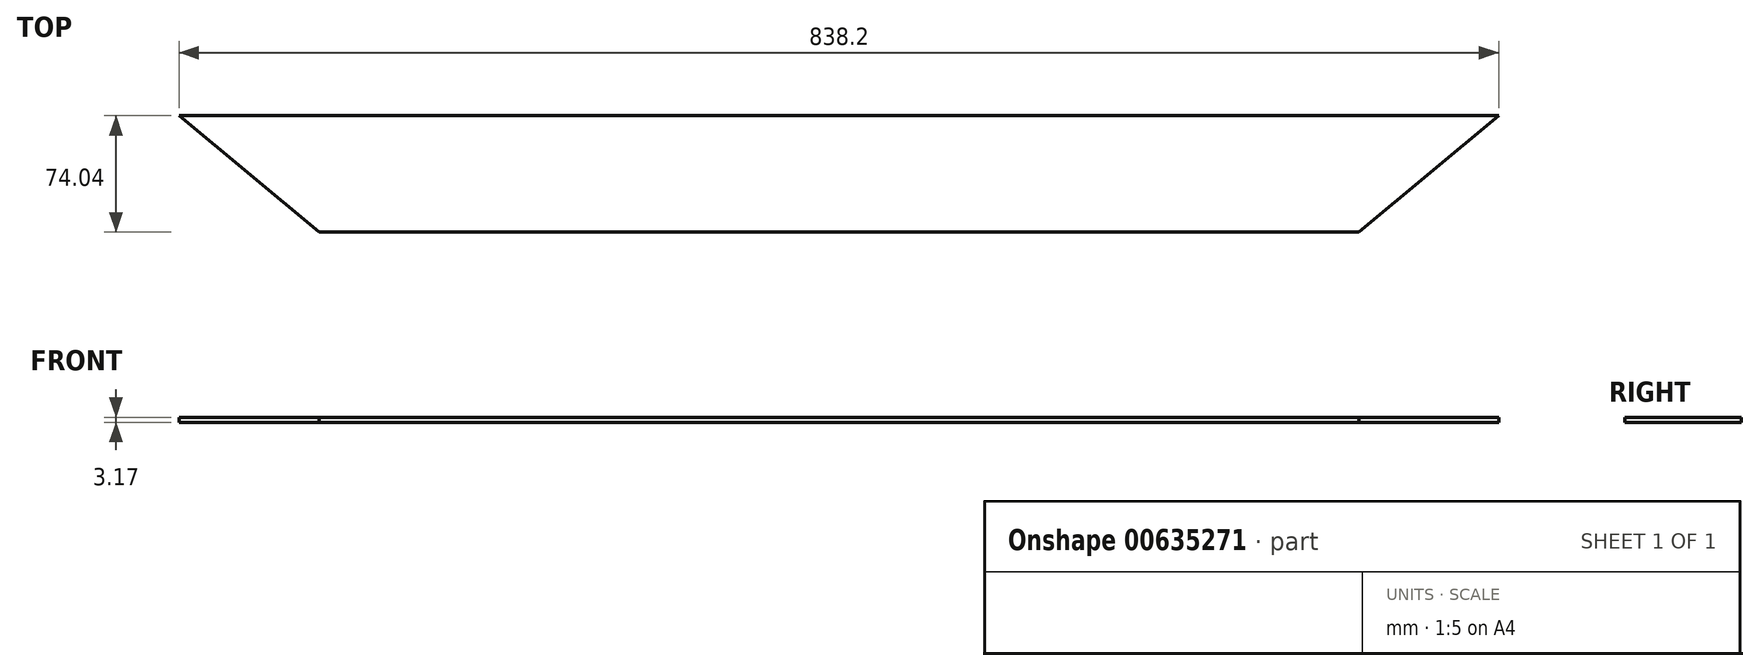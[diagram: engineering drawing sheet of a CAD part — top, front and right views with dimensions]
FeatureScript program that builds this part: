
annotation { "Feature Type Name" : "Feature", "Feature Type Description" : "" }
export const myFeature = defineFeature(function(context is Context, id is Id, definition is map)
    precondition{}
    {
        {
            var Q0;
            Q0=qCreatedBy(makeId("Top.planeOp"),FACE);
            var sketch = newSketch(context, id + "F0", { "sketchPlane" : qUnion([Q0])});
            skLineSegment(sketch, "E0.bottom", {"start": v(330.2, 37.02) * mm, "end": v(-330.2, 37.02) * mm});
            skLineSegment(sketch, "E0.top", {"start": v(330.2, -37.02) * mm, "end": v(-330.2, -37.02) * mm});
            skLineSegment(sketch, "E0.left", {"start": v(330.2, 37.02) * mm, "end": v(330.2, -37.02) * mm});
            skLineSegment(sketch, "E0.right", {"start": v(-330.2, 37.02) * mm, "end": v(-330.2, -37.02) * mm});
            skPoint(sketch, "E0.middle", {"position": v(0, 0) * mm});
            skLineSegment(sketch, "E1", {"start": v(-330.2, -37.02) * mm, "end": v(-419.1, 37.02) * mm});
            skLineSegment(sketch, "E2", {"start": v(-419.1, 37.02) * mm, "end": v(-330.2, 37.02) * mm});
            skLineSegment(sketch, "E3", {"start": v(330.2, -37.02) * mm, "end": v(419.1, 37.02) * mm});
            skLineSegment(sketch, "E4", {"start": v(419.1, 37.02) * mm, "end": v(330.2, 37.02) * mm});
            skSolve(sketch);
        }
        {
            var Q0;
            Q0 = qSketchRegion(id + "F0", true);
            extrude(context, id + "F1", {"entities" : qUnion([Q0]), "depth" : 3.17 * mm, "offsetDistance" : 25.4 * mm});
        }
    });
